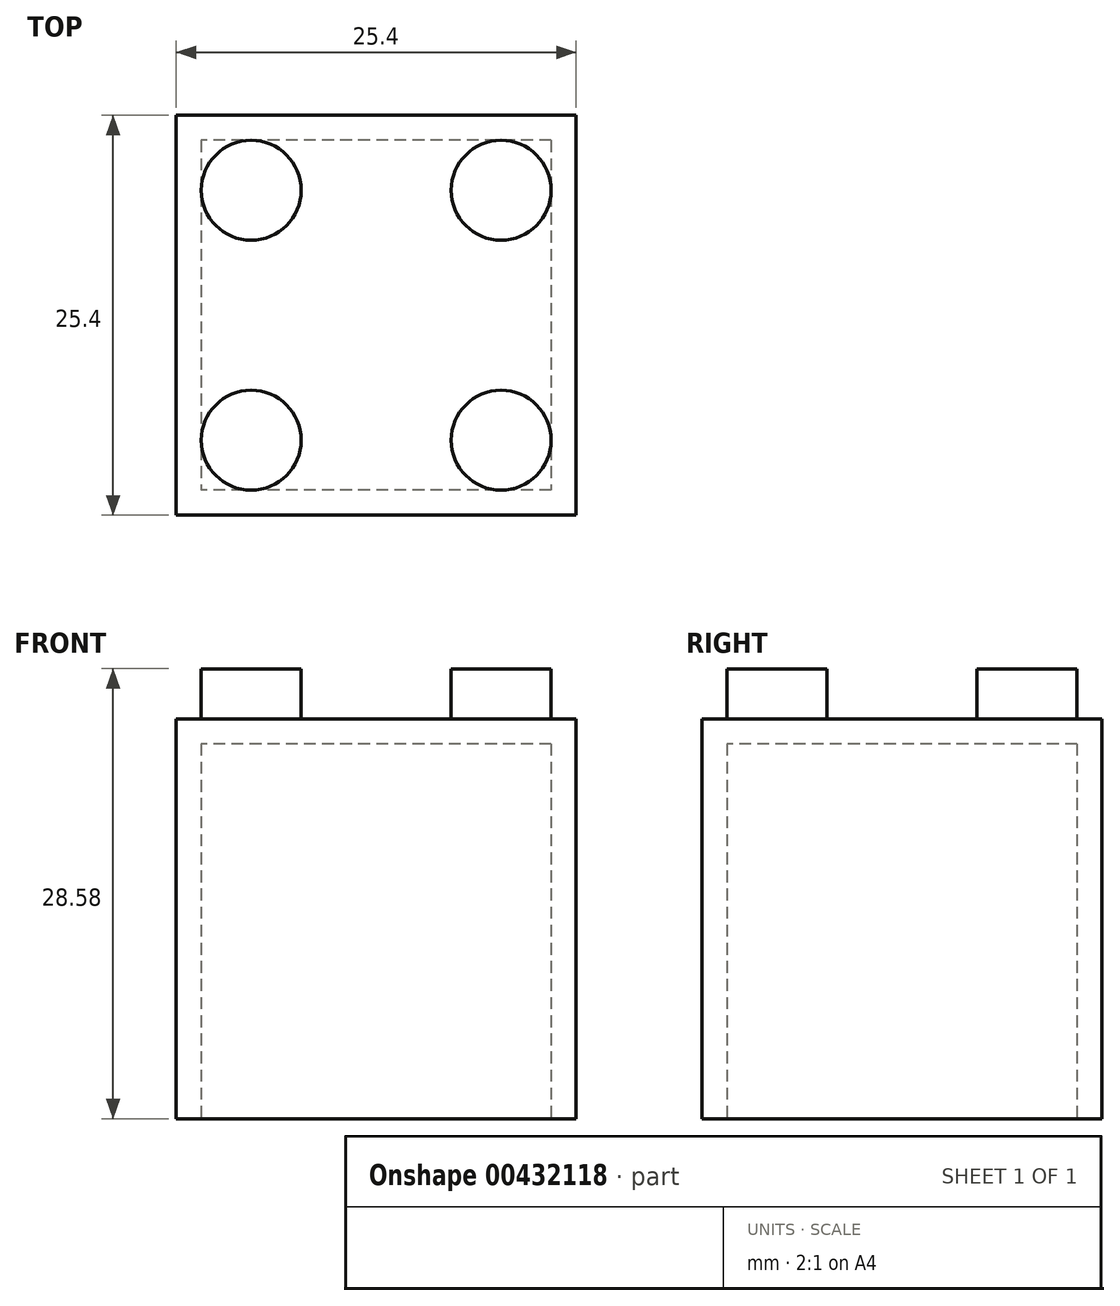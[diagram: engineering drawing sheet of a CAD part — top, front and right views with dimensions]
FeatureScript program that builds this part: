
annotation { "Feature Type Name" : "Feature", "Feature Type Description" : "" }
export const myFeature = defineFeature(function(context is Context, id is Id, definition is map)
    precondition{}
    {
        {
            var Q0;
            Q0=qCreatedBy(makeId("Top.planeOp"),FACE);
            var sketch = newSketch(context, id + "F0", { "sketchPlane" : qUnion([Q0])});
            skLineSegment(sketch, "E0.bottom", {"start": v(12.7, 25.4) * mm, "end": v(-12.7, 25.4) * mm});
            skLineSegment(sketch, "E0.top", {"start": v(12.7, 0) * mm, "end": v(-12.7, 0) * mm});
            skLineSegment(sketch, "E0.left", {"start": v(12.7, 25.4) * mm, "end": v(12.7, 0) * mm});
            skLineSegment(sketch, "E0.right", {"start": v(-12.7, 25.4) * mm, "end": v(-12.7, 0) * mm});
            skLineSegment(sketch, "E1.bottom", {"start": v(11.11, 23.81) * mm, "end": v(-11.11, 23.81) * mm});
            skLineSegment(sketch, "E1.top", {"start": v(11.11, 1.59) * mm, "end": v(-11.11, 1.59) * mm});
            skLineSegment(sketch, "E1.left", {"start": v(11.11, 23.81) * mm, "end": v(11.11, 1.59) * mm});
            skLineSegment(sketch, "E1.right", {"start": v(-11.11, 23.81) * mm, "end": v(-11.11, 1.59) * mm});
            skPoint(sketch, "E2", {"position": v(0, 0) * mm});
            skPoint(sketch, "E3", {"position": v(0, 1.59) * mm});
            skSolve(sketch);
        }
        {
            var Q0;
            Q0=makeQuery(id+"F0.imprint","IMPRINT",FACE,{"disambiguationData":[TD([[makeQuery(id+"F0.imprint","IMPRINT",EDGE,{"derivedFrom":sQuery(id+"F0.wireOp",EDGE,"E1.bottom")}),1.0]])]});
            var Q1;
            Q1=makeQuery(id+"F0.imprint","IMPRINT",FACE,{"disambiguationData":[TD([[makeQuery(id+"F0.imprint","IMPRINT",EDGE,{"derivedFrom":sQuery(id+"F0.wireOp",EDGE,"E0.bottom")}),1.0]])]});
            extrude(context, id + "F1", {"entities" : qUnion([Q0, Q1]), "depth" : 25.4 * mm});
        }
        {
            var Q0;
            Q0=makeQuery(id+"F0.imprint","IMPRINT",FACE,{"disambiguationData":[TD([[makeQuery(id+"F0.imprint","IMPRINT",EDGE,{"derivedFrom":sQuery(id+"F0.wireOp",EDGE,"E1.bottom")}),1.0]])]});
            extrude(context, id + "F2", {"entities" : qUnion([Q0]), "operationType" : NewBodyOperationType.REMOVE, "depth" : 23.8 * mm});
        }
        {
            var Q0;
            Q0=makeQuery(id+"F1.opExtrude","CAP_FACE",FACE,{"disambiguationData":[OSD([sQuery(id+"F0.wireOp",EDGE,"E0.bottom"),sQuery(id+"F0.wireOp",EDGE,"E0.top"),sQuery(id+"F0.wireOp",EDGE,"E0.left"),sQuery(id+"F0.wireOp",EDGE,"E0.right")])],"isStart":false});
            var sketch = newSketch(context, id + "F3", { "sketchPlane" : qUnion([Q0])});
            skCircle(sketch, "E4", {"center": v(7.94, 4.76) * mm, "radius": 3.18 * mm});
            skCircle(sketch, "E5", {"center": v(-7.94, 20.64) * mm, "radius": 3.18 * mm});
            skCircle(sketch, "E6", {"center": v(7.94, 20.64) * mm, "radius": 3.18 * mm});
            skCircle(sketch, "E7", {"center": v(-7.94, 4.76) * mm, "radius": 3.18 * mm});
            skLineSegment(sketch, "E8", {"start": v(7.94, 20.64) * mm, "end": v(7.94, 4.76) * mm, "construction": true});
            skLineSegment(sketch, "E9", {"start": v(7.94, 20.64) * mm, "end": v(-7.94, 20.64) * mm, "construction": true});
            skLineSegment(sketch, "E10", {"start": v(-7.94, 4.76) * mm, "end": v(-7.94, 20.64) * mm, "construction": true});
            skLineSegment(sketch, "E11", {"start": v(-7.94, 4.76) * mm, "end": v(7.94, 4.76) * mm, "construction": true});
            skSolve(sketch);
        }
        {
            var Q0;
            Q0=makeQuery(id+"F3.imprint","IMPRINT",FACE,{"disambiguationData":[TD([[makeQuery(id+"F3.imprint","IMPRINT",EDGE,{"derivedFrom":sQuery(id+"F3.wireOp",EDGE,"E4")}),1.0]])]});
            var Q1;
            Q1=makeQuery(id+"F3.imprint","IMPRINT",FACE,{"disambiguationData":[TD([[makeQuery(id+"F3.imprint","IMPRINT",EDGE,{"derivedFrom":sQuery(id+"F3.wireOp",EDGE,"E6")}),1.0]])]});
            var Q2;
            Q2=makeQuery(id+"F3.imprint","IMPRINT",FACE,{"disambiguationData":[TD([[makeQuery(id+"F3.imprint","IMPRINT",EDGE,{"derivedFrom":sQuery(id+"F3.wireOp",EDGE,"E5")}),1.0]])]});
            var Q3;
            Q3=makeQuery(id+"F3.imprint","IMPRINT",FACE,{"disambiguationData":[TD([[makeQuery(id+"F3.imprint","IMPRINT",EDGE,{"derivedFrom":sQuery(id+"F3.wireOp",EDGE,"E7")}),1.0]])]});
            extrude(context, id + "F4", {"entities" : qUnion([Q0, Q1, Q2, Q3]), "operationType" : NewBodyOperationType.ADD, "depth" : 3.17 * mm});
        }
    });
